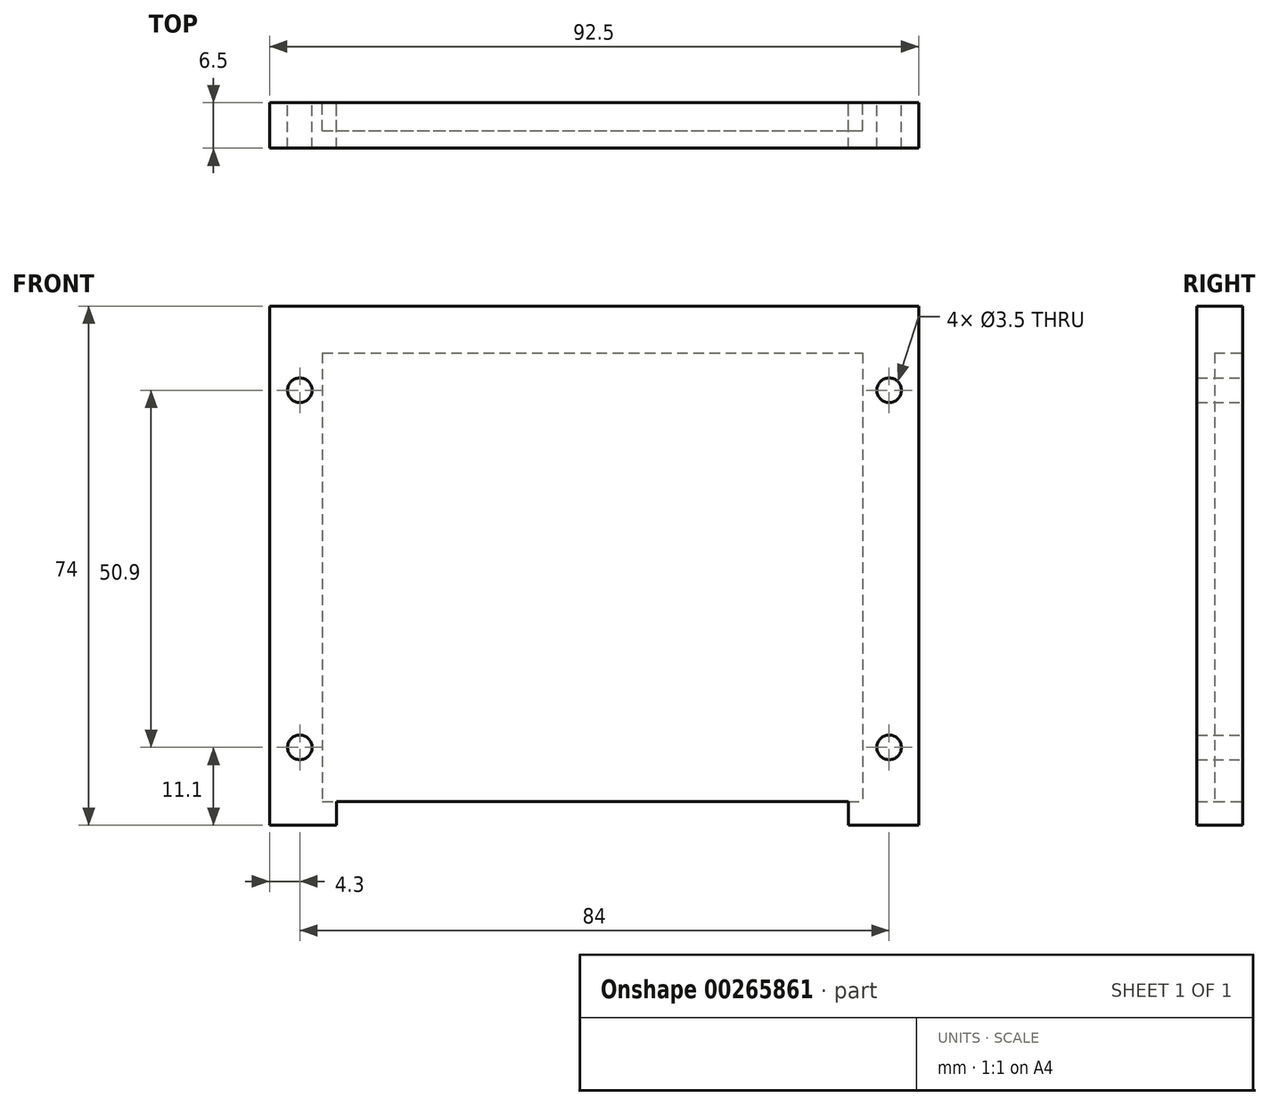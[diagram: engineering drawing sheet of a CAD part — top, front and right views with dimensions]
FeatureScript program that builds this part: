
annotation { "Feature Type Name" : "Feature", "Feature Type Description" : "" }
export const myFeature = defineFeature(function(context is Context, id is Id, definition is map)
    precondition{}
    {
        {
            var Q0;
            Q0=qCreatedBy(makeId("Front.planeOp"),FACE);
            var sketch = newSketch(context, id + "F0", { "sketchPlane" : qUnion([Q0])});
            skLineSegment(sketch, "E0.bottom", {"start": v(-38.2, 29.95) * mm, "end": v(38.8, 29.95) * mm});
            skLineSegment(sketch, "E0.top", {"start": v(-38.2, -34.05) * mm, "end": v(38.8, -34.05) * mm});
            skLineSegment(sketch, "E0.left", {"start": v(-38.2, 29.95) * mm, "end": v(-38.2, -34.05) * mm});
            skLineSegment(sketch, "E0.right", {"start": v(38.8, 29.95) * mm, "end": v(38.8, -34.05) * mm});
            skLineSegment(sketch, "E1.bottom", {"start": v(-35.75, 26.9) * mm, "end": v(35.7, 26.9) * mm});
            skLineSegment(sketch, "E1.top", {"start": v(-35.75, -26.95) * mm, "end": v(35.7, -26.95) * mm});
            skLineSegment(sketch, "E1.left", {"start": v(-35.75, 26.9) * mm, "end": v(-35.75, -26.95) * mm});
            skLineSegment(sketch, "E1.right", {"start": v(35.7, 26.9) * mm, "end": v(35.7, -26.95) * mm});
            skPoint(sketch, "E2", {"position": v(-41.4, 24.6) * mm});
            skPoint(sketch, "E3", {"position": v(-41.4, -26.3) * mm});
            skPoint(sketch, "E4", {"position": v(42.6, 24.6) * mm});
            skPoint(sketch, "E5", {"position": v(42.6, -26.3) * mm});
            skLineSegment(sketch, "E6.bottom", {"start": v(-45.7, 36.6) * mm, "end": v(46.8, 36.6) * mm});
            skLineSegment(sketch, "E6.top", {"start": v(-45.7, -37.4) * mm, "end": v(46.8, -37.4) * mm});
            skLineSegment(sketch, "E6.left", {"start": v(-45.7, 36.6) * mm, "end": v(-45.7, -37.4) * mm});
            skLineSegment(sketch, "E6.right", {"start": v(46.8, 36.6) * mm, "end": v(46.8, -37.4) * mm});
            skLineSegment(sketch, "E7", {"start": v(36.8, -34.05) * mm, "end": v(36.8, -37.4) * mm});
            skLineSegment(sketch, "E8", {"start": v(-36.2, -34.05) * mm, "end": v(-36.2, -37.4) * mm});
            skSolve(sketch);
        }
        {
            var Q0;
            Q0=makeQuery(id+"F0.imprint","IMPRINT",FACE,{"disambiguationData":[TD([[makeQuery(id+"F0.imprint","IMPRINT",EDGE,{"derivedFrom":sQuery(id+"F0.wireOp",EDGE,"E0.bottom")}),1.0]])]});
            var Q1;
            Q1=makeQuery(id+"F0.imprint","IMPRINT",FACE,{"disambiguationData":[TD([[makeQuery(id+"F0.imprint","IMPRINT",EDGE,{"derivedFrom":sQuery(id+"F0.wireOp",EDGE,"E0.bottom")}),-1.0]])]});
            var Q2;
            Q2=makeQuery(id+"F0.imprint","IMPRINT",FACE,{"disambiguationData":[TD([[makeQuery(id+"F0.imprint","IMPRINT",EDGE,{"derivedFrom":sQuery(id+"F0.wireOp",EDGE,"E1.bottom")}),-1.0]])]});
            extrude(context, id + "F1", {"entities" : qUnion([Q0, Q1, Q2]), "depth" : 6.5 * mm});
        }
        {
            var Q0;
            Q0=makeQuery(id+"F0.imprint","IMPRINT",FACE,{"disambiguationData":[TD([[makeQuery(id+"F0.imprint","IMPRINT",EDGE,{"derivedFrom":sQuery(id+"F0.wireOp",EDGE,"E1.bottom")}),-1.0]])]});
            var Q1;
            Q1=makeQuery(id+"F0.imprint","IMPRINT",FACE,{"disambiguationData":[TD([[makeQuery(id+"F0.imprint","IMPRINT",EDGE,{"derivedFrom":sQuery(id+"F0.wireOp",EDGE,"E0.bottom")}),-1.0]])]});
            var Q2;
            {var subQ0=sQuery(id+"F0.wireOp",EDGE,"E7");Q2=makeQuery(id+"F0.imprint","IMPRINT",FACE,{"disambiguationData":[TD([[makeQuery(id+"F0.imprint","IMPRINT",EDGE,{"derivedFrom":subQ0}),-1.0]])]});}
            extrude(context, id + "F2", {"entities" : qUnion([Q0, Q1, Q2]), "operationType" : NewBodyOperationType.REMOVE, "depth" : 4 * mm});
        }
        {
            var Q0;
            Q0=sQuery(id+"F0.wireOp",VERTEX,"E2");
            var Q1;
            Q1=sQuery(id+"F0.wireOp",VERTEX,"E4");
            var Q2;
            Q2=sQuery(id+"F0.wireOp",VERTEX,"E5");
            var Q3;
            Q3=sQuery(id+"F0.wireOp",VERTEX,"E3");
            var Q4;
            Q4=makeQuery(id+"F1.opExtrude","SWEPT_BODY",BODY,{"disambiguationData":[OSD([sQuery(id+"F0.wireOp",EDGE,"E0.top"),sQuery(id+"F0.wireOp",EDGE,"E6.bottom"),sQuery(id+"F0.wireOp",EDGE,"E6.top"),sQuery(id+"F0.wireOp",EDGE,"E6.left"),sQuery(id+"F0.wireOp",EDGE,"E6.right"),sQuery(id+"F0.wireOp",EDGE,"E7"),sQuery(id+"F0.wireOp",EDGE,"E8")])]});
            hole(context, id + "F3", {"style" : HoleStyle.SIMPLE, "endStyle" : HoleEndStyle.THROUGH, "oppositeDirection" : true, "holeDiameter" : 3.5 * mm, "tappedDepth" : 12 * mm, "tapClearance" : 3, "locations" : qUnion([Q0, Q1, Q2, Q3]), "scope" : qUnion([Q4])});
        }
    });
